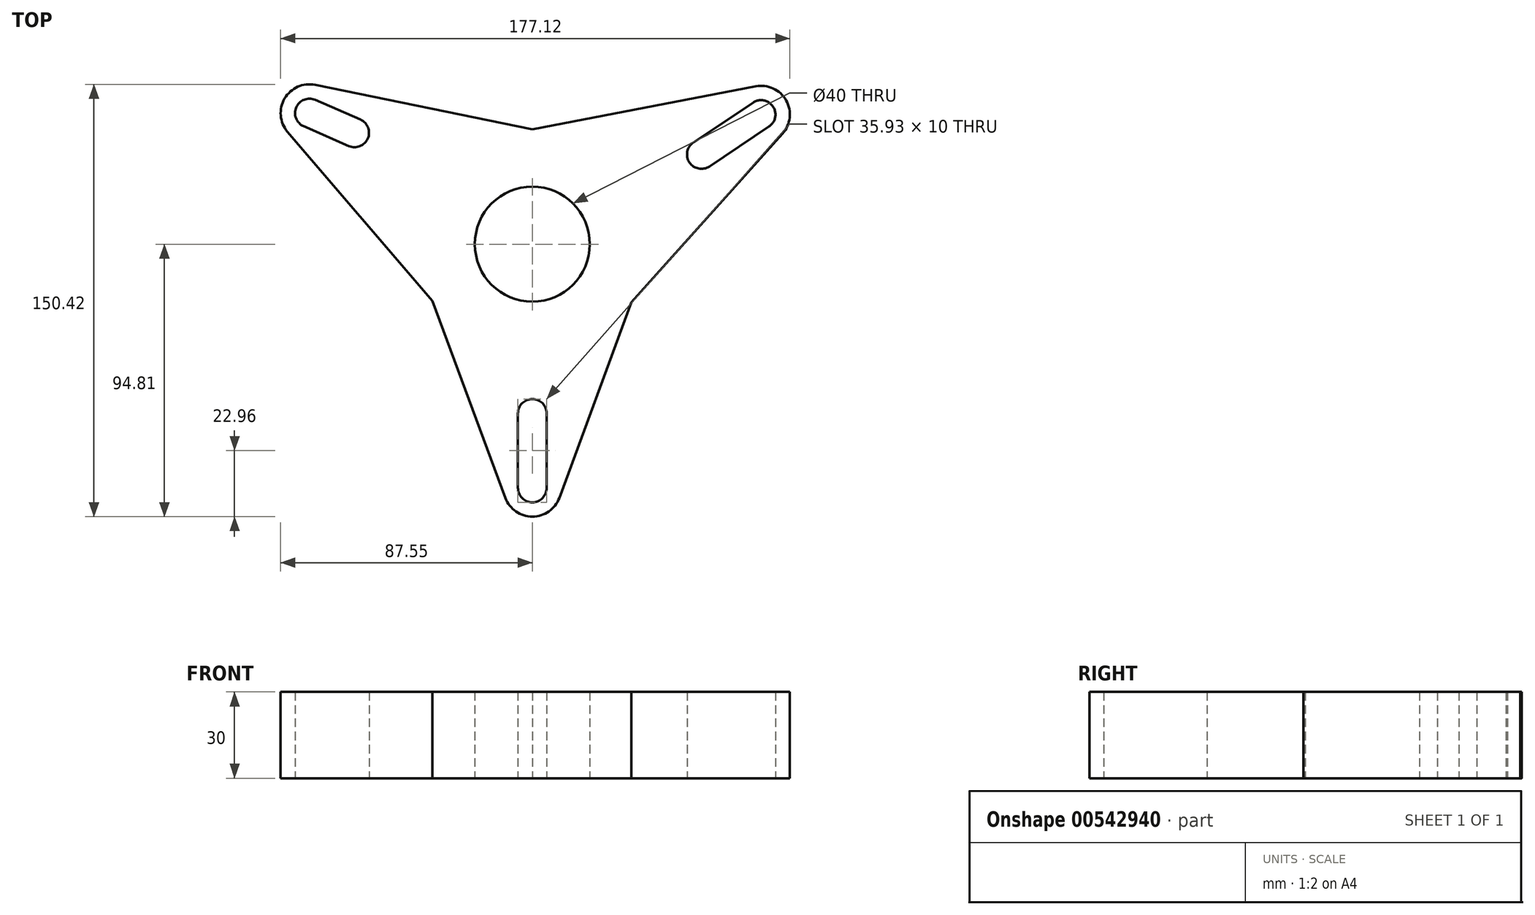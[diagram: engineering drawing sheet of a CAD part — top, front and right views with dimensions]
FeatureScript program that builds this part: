
annotation { "Feature Type Name" : "Feature", "Feature Type Description" : "" }
export const myFeature = defineFeature(function(context is Context, id is Id, definition is map)
    precondition{}
    {
        {
            var Q0;
            Q0=qCreatedBy(makeId("Top.planeOp"),FACE);
            var sketch = newSketch(context, id + "F0", { "sketchPlane" : qUnion([Q0])});
            skCircle(sketch, "E0", {"center": v(0, 0) * mm, "radius": 20 * mm});
            skCircle(sketch, "E1", {"center": v(0, 0) * mm, "radius": 40 * mm});
            skLineSegment(sketch, "E2", {"start": v(0, 0) * mm, "end": v(0, 40) * mm});
            skLineSegment(sketch, "E3", {"start": v(0, 0) * mm, "end": v(0, -40) * mm});
            skArc(sketch, "E4", {"start": v(-75.55, 55.4) * mm, "mid": v(-86.17, 50.68) * mm, "end": v(-85.15, 39.1) * mm});
            skArc(sketch, "E5", {"start": v(87.03, 38.42) * mm, "mid": v(88.28, 50.02) * mm, "end": v(77.69, 54.91) * mm});
            skArc(sketch, "E6", {"start": v(-9.38, -88.3) * mm, "mid": v(0, -94.81) * mm, "end": v(9.38, -88.28) * mm});
            skLineSegment(sketch, "E7", {"start": v(-85.15, 39.1) * mm, "end": v(-34.8, -19.72) * mm});
            skLineSegment(sketch, "E8", {"start": v(-34.8, -19.72) * mm, "end": v(-9.38, -88.3) * mm});
            skLineSegment(sketch, "E9", {"start": v(9.38, -88.28) * mm, "end": v(34.48, -20.28) * mm});
            skLineSegment(sketch, "E10", {"start": v(34.48, -20.28) * mm, "end": v(87.03, 38.42) * mm});
            skLineSegment(sketch, "E11", {"start": v(77.69, 54.91) * mm, "end": v(0, 40) * mm});
            skLineSegment(sketch, "E12", {"start": v(0, 40) * mm, "end": v(-75.55, 55.4) * mm});
            skArc(sketch, "E13", {"start": v(-75.55, 50.2) * mm, "mid": v(-82.14, 47.61) * mm, "end": v(-79.55, 41.03) * mm});
            skArc(sketch, "E14", {"start": v(82.35, 40.94) * mm, "mid": v(83.73, 47.87) * mm, "end": v(76.8, 49.25) * mm});
            skArc(sketch, "E15", {"start": v(-5, -84.81) * mm, "mid": v(0, -89.81) * mm, "end": v(5, -84.81) * mm});
            skArc(sketch, "E16", {"start": v(5, -58.89) * mm, "mid": v(0, -53.89) * mm, "end": v(-5, -58.89) * mm});
            skArc(sketch, "E17", {"start": v(-63.81, 34.16) * mm, "mid": v(-57.23, 36.75) * mm, "end": v(-59.81, 43.33) * mm});
            skArc(sketch, "E18", {"start": v(56.03, 35.37) * mm, "mid": v(54.66, 28.43) * mm, "end": v(61.6, 27.05) * mm});
            skLineSegment(sketch, "E19", {"start": v(-75.55, 50.2) * mm, "end": v(-59.81, 43.33) * mm});
            skLineSegment(sketch, "E20", {"start": v(-79.55, 41.03) * mm, "end": v(-63.81, 34.16) * mm});
            skLineSegment(sketch, "E21", {"start": v(56.03, 35.37) * mm, "end": v(76.8, 49.25) * mm});
            skLineSegment(sketch, "E22", {"start": v(82.35, 40.94) * mm, "end": v(61.6, 27.05) * mm});
            skLineSegment(sketch, "E23", {"start": v(-5, -58.89) * mm, "end": v(-5, -84.81) * mm});
            skLineSegment(sketch, "E24", {"start": v(5, -58.89) * mm, "end": v(5, -84.81) * mm});
            skSolve(sketch);
        }
        {
            var Q0;
            Q0=makeQuery(id+"F0.imprint","IMPRINT",FACE,{"disambiguationData":[TD([[makeQuery(id+"F0.imprint","IMPRINT",EDGE,{"derivedFrom":sQuery(id+"F0.wireOp",EDGE,"E6")}),1.0]])]});
            var Q1;
            {var subQ4=sQuery(id+"F0.wireOp",EDGE,"E2");var subQ6=sQuery(id+"F0.wireOp",EDGE,"E0");var subQ7=makeQuery(id+"F0.imprint","INTERSECT",VERTEX,{"derivedFrom":[subQ6,subQ4]});Q1=makeQuery(id+"F0.imprint","IMPRINT",FACE,{"disambiguationData":[TD([[makeQuery(id+"F0.imprint","IMPRINT",EDGE,{"disambiguationData":[TD([[subQ7,-1.0]])],"derivedFrom":subQ6}),-1.0]])]});}
            var Q2;
            {var subQ0=sQuery(id+"F0.wireOp",EDGE,"E2");var subQ3=sQuery(id+"F0.wireOp",EDGE,"E0");var subQ4=makeQuery(id+"F0.imprint","INTERSECT",VERTEX,{"derivedFrom":[subQ3,subQ0]});Q2=makeQuery(id+"F0.imprint","IMPRINT",FACE,{"disambiguationData":[TD([[makeQuery(id+"F0.imprint","IMPRINT",EDGE,{"disambiguationData":[TD([[subQ4,1.0]])],"derivedFrom":subQ3}),-1.0]])]});}
            var Q3;
            Q3=makeQuery(id+"F0.imprint","IMPRINT",FACE,{"disambiguationData":[TD([[makeQuery(id+"F0.imprint","IMPRINT",EDGE,{"derivedFrom":sQuery(id+"F0.wireOp",EDGE,"E4")}),1.0]])]});
            var Q4;
            Q4=makeQuery(id+"F0.imprint","IMPRINT",FACE,{"disambiguationData":[TD([[makeQuery(id+"F0.imprint","IMPRINT",EDGE,{"derivedFrom":sQuery(id+"F0.wireOp",EDGE,"E5")}),1.0]])]});
            extrude(context, id + "F1", {"entities" : qUnion([Q0, Q1, Q2, Q3, Q4]), "depth" : 30 * mm, "offsetDistance" : 25 * mm});
        }
    });
